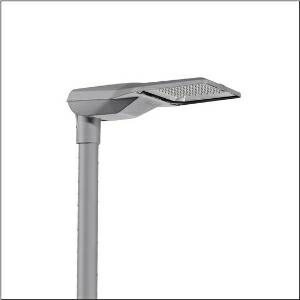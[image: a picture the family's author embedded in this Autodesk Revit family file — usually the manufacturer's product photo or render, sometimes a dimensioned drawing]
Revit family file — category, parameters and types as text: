
# Revit family: streetlight_sl_21_iq_midi___st1_0a_5xe3d41d08mb_7520
name_source: partatom
category: Lighting Fixtures
units: mm (PartAtom-declared; Revit-internal decimal feet)

## family parameters
Cut with Voids When Loaded = No
Host = Face
Light Source = No
Part Type = Normal
Room Calculation Point = No
Round Connector Dimension = Use Diameter
Shared = No

## types (1)
- --- (1 x LED, 20360 lm, 146.7 W, 4000K)
    Apparent Load = 147 VA
    CIE Flux Codes = 37 72 97 100 100
    Color Rendering = 70
    Color Temperature = 4000K
    Default Elevation = 1800 mm
    Description = Streetlight SL 21 iQ midi, mast luminaire, primary light control with lens, of PMMA, primary optical cover: cover, of toughened safety glass, transparent, light distribution: ST1.0a, light emission: direct distribution, primary light characteristic: asymmetric, installation type: post-top, side-entry, LED, High Power LED, rated luminous flux: 20.360lm, luminous efficacy: 139lm/W, light colour: 740, colour temperature: 4000K, control gear: iQ-Comfort, control: Auto-Match, Temp-Guard, Lumen-Switch, Night-Set, Smart-Wire, Light-Fading, Desk-Remote (wireless, voltage-free reading and setting of iQ features in the workshop via application-optimized NFC function/RFID function), optimised constant luminous flux control (CLO 2.0), pre-setting: linear dimming characteristic, mains connection: 230..240V, AC, 50/60Hz, start of lifetime: 147W, end of service life: 161W, reduction: 62W, luminaire housing, of diecast aluminium, powder-coated, SITECO metallic grey (DB 702S), corrosivity category C5 high according to DIN EN ISO 12944, please order mast flange separately, inclination adjustable: 0°, 5°, 10°, 15°, sealing non-destructively replaceable, multi-level sealing system, length: 644mm, width: 335mm, height: 110mm, mast flange for spigot size: 42mm (side-entry): 5XC10008XM4, 60/48mm (side-entry/post-top): 5XC10108XM2, 76/60mm (side-entry/post-top): 5XC10108XM1, mounting height: 4..8m, protection rating (complete): IP66, insulation class (complete): insulation class II (safety insulation), certification: CE, ENEC, ENEC+, VDE, impact resistance: IK10, permissible operating ambient temperature for outdoor applications: -40..+50°C, standard-compliant lighting for roads and squares, packaging unit: 1 piece

Light Distribution: ST1.0a
    Height = 111 mm
    Lamp = 1 x LED
    Lamp Light Flux = 20360 lm
    Lamp Power = 146.7 W
    Lamp count = 1
    Length = 644 mm
    Luminous efficacy = 139 lm/W
    Manufacturer = Siteco
    ModVariant = No
    Model = 5XE3D41D08MB
    Number of Poles = 1
    OnlyDefault = Yes
    Power Factor = 1
    Product Name = Streetlight SL 21 iQ midi | ST1.0a
    Product group = mast luminaire | pylon top
    ProductGroupID = 6100
    Protection Class = Protection class II
    Protection Degree = IP 66
    RLX_Detail_Level = 1
    RLX_Emergency_Light_Flux = 0 lm
    RLX_Emergency_Type = 0
    RLX_Emergency_Type_DB = No
    RlxData = <blob elided: 26861 chars, md5=e8a9dd6f>
    Socket = socket
    Standby Power = 0 W
    System Light Flux = 20360 lm
    System Power = 147 W
    Type Comments = factory setting: luminous flux: 100 % | dim-lin: 254 | 753 mA
    Type Image = l_1004298.jpg
    URL = http://relux.com
    VarID = @adj_186921
    Voltage = 0 V
    Weight = 0.00 kg
    Width = 336 mm

## geometry (parser evidence)
native form markers: Blend x4, Sweep x11
no freeform markers — native parametric forms only
